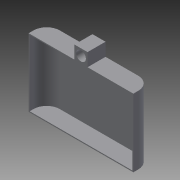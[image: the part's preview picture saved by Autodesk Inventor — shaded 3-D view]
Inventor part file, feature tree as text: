
AUTODESK INVENTOR PART (.ipt)
format: ipt  version: 2015 SP1 (Build 190203100, 203)  size: 124,416 bytes
history: native  units: in
note: dims shown in document units (in); Inventor stores cm internally (conversion verified against a paired STEP export)
features: sketch x3, extrude x2, fillet x2, projected_geometry x2, shell x1, hole x1
ambient origin geometry x8: Origin, YZ Plane, XZ Plane, XY Plane, X Axis, Y Axis, Z Axis, Center Point
bodies: Solid1 (feature_tree)
feature tree (11):
  extrude  "Extrusion1"  Depth=2.2677in
  shell  "Shell1"  Thickness=2.7008in
  fillet  "Fillet1"  Radius=2.1024in
  extrude  "Extrusion2"  Depth=0.6875in TaperAngle=0.0deg
  hole  "Hole1"  [1 undecoded]
  fillet  "Fillet2"  Radius=0.0394in
  sketch  "Sketch1"  dims[d0=1.7008in d1=2.2677in d2=2.7008in d3=2.1024in]
  sketch  "Sketch2"  dims[d4=0.25in d5=0.6875in d6=0.0in]
  projected_geometry  "Projected Loop1"
  sketch  "Sketch3"  dims[d7=4.0in d8=2.6024in d9=0.0394in d10=0.5in d11=0.5in d13=0.5in d14=0.0in d15=0.375in d16=0.75in d17=0.375in d18=0.25in d19=0.5635in d20=1.0in d21=0.8108in d22=0.5in]
  projected_geometry  "Projected Loop2"
note: 1 required parameter value undecoded (feature->parameter linkage not recoverable at this tier; creation-order binding heuristic only, values carry confidence <= 0.55)
